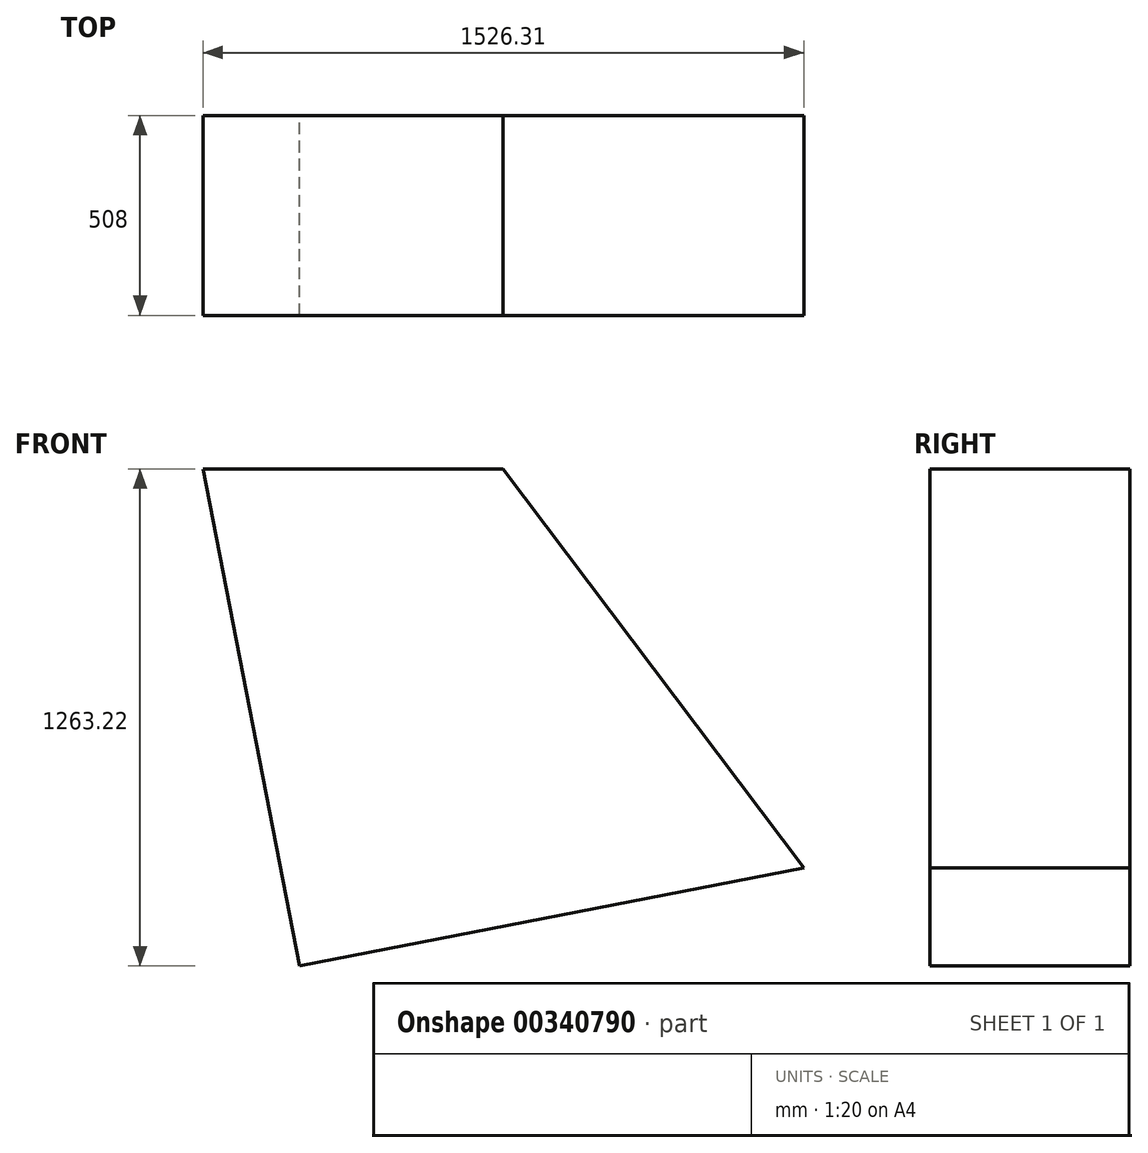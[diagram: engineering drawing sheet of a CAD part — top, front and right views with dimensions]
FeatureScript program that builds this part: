
annotation { "Feature Type Name" : "Feature", "Feature Type Description" : "" }
export const myFeature = defineFeature(function(context is Context, id is Id, definition is map)
    precondition{}
    {
        {
            var Q0;
            Q0=qCreatedBy(makeId("Front.planeOp"),FACE);
            var sketch = newSketch(context, id + "F0", { "sketchPlane" : qUnion([Q0])});
            skLineSegment(sketch, "E0", {"start": v(0, 0) * mm, "end": v(762, 0) * mm});
            skLineSegment(sketch, "E1", {"start": v(762, 0) * mm, "end": v(1526.3, -1014.27) * mm});
            skLineSegment(sketch, "E2", {"start": v(1526.3, -1014.27) * mm, "end": v(245.55, -1263.22) * mm});
            skLineSegment(sketch, "E3", {"start": v(245.55, -1263.22) * mm, "end": v(0, 0) * mm});
            skSolve(sketch);
        }
        {
            var Q0;
            Q0=makeQuery(id+"F0.imprint","IMPRINT",FACE,{"disambiguationData":[TD([[makeQuery(id+"F0.imprint","IMPRINT",EDGE,{"derivedFrom":sQuery(id+"F0.wireOp",EDGE,"E0")}),-1.0]])]});
            extrude(context, id + "F1", {"entities" : qUnion([Q0]), "depth" : 508 * mm});
        }
    });
